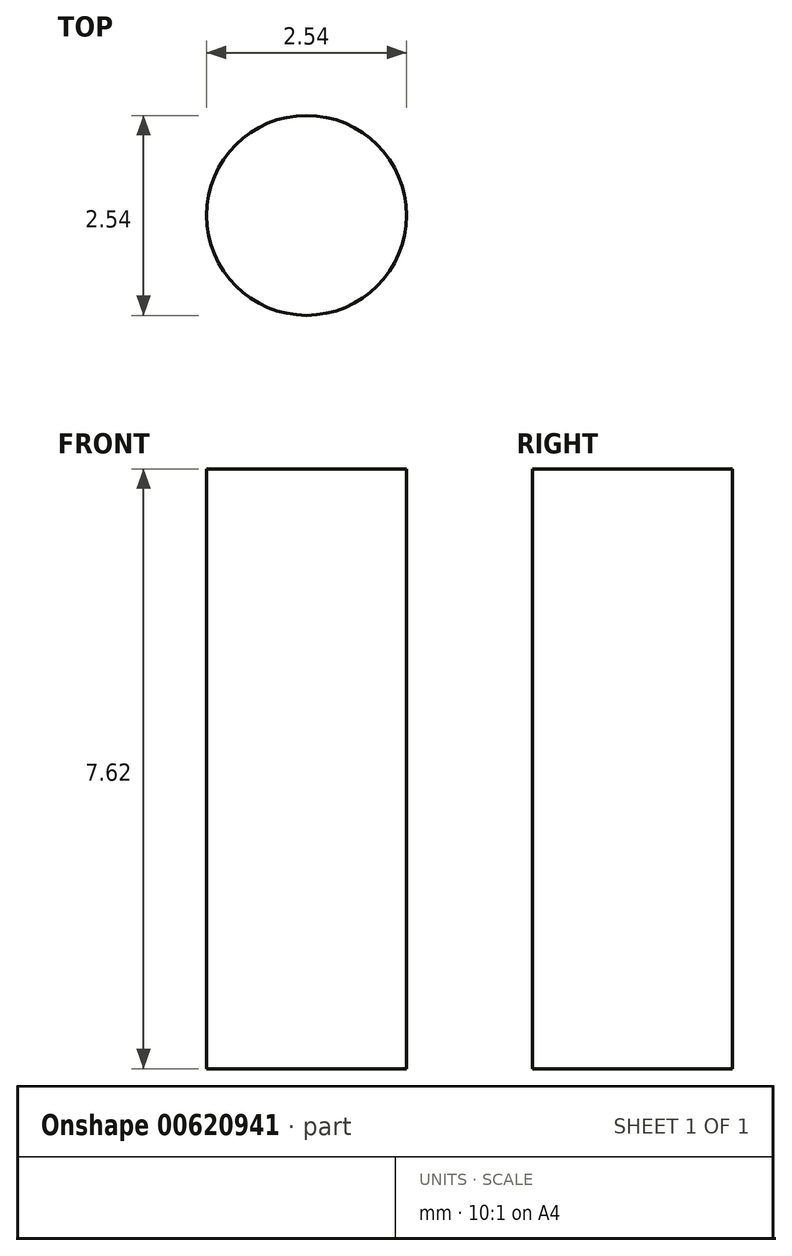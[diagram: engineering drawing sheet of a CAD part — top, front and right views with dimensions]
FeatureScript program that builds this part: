
annotation { "Feature Type Name" : "Feature", "Feature Type Description" : "" }
export const myFeature = defineFeature(function(context is Context, id is Id, definition is map)
    precondition{}
    {
        {
            var Q0;
            Q0=qCreatedBy(makeId("Top.planeOp"),FACE);
            var sketch = newSketch(context, id + "F0", { "sketchPlane" : qUnion([Q0])});
            skCircle(sketch, "E0", {"center": v(0, 0) * mm, "radius": 1.27 * mm});
            skSolve(sketch);
        }
        {
            var Q0;
            Q0=qSketchRegion(id+"F0",true);
            extrude(context, id + "F1", {"entities" : qUnion([Q0]), "depth" : 7.62 * mm, "offsetDistance" : 25.4 * mm});
        }
    });
